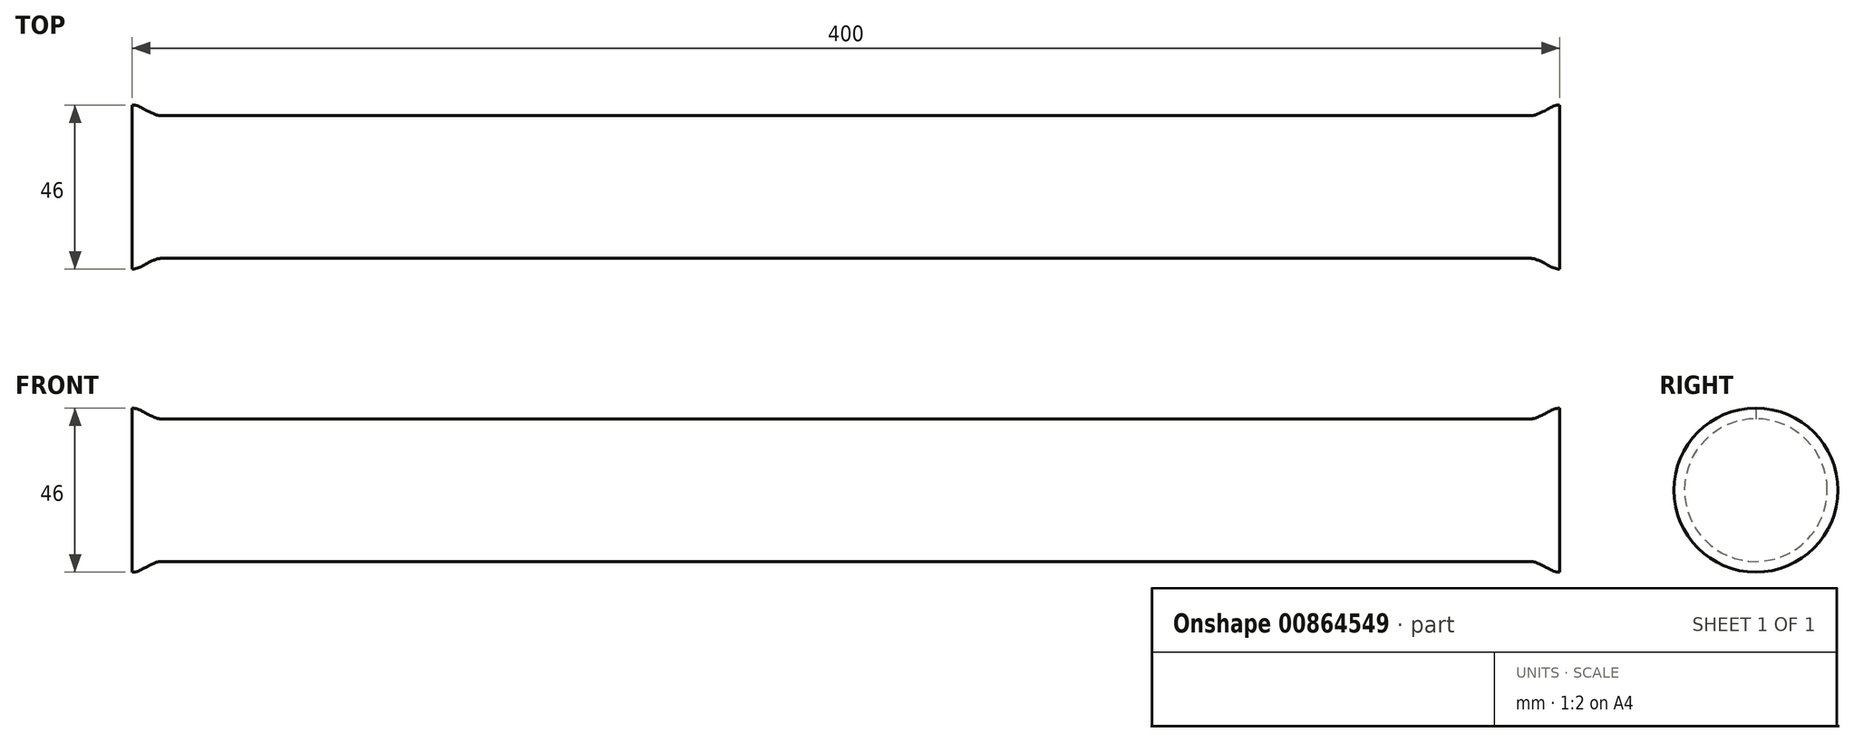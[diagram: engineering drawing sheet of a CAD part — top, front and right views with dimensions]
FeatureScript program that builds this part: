
annotation { "Feature Type Name" : "Feature", "Feature Type Description" : "" }
export const myFeature = defineFeature(function(context is Context, id is Id, definition is map)
    precondition{}
    {
        {
            var Q0;
            Q0=qCreatedBy(makeId("Front.planeOp"),FACE);
            var sketch = newSketch(context, id + "F0", { "sketchPlane" : qUnion([Q0])});
            skLineSegment(sketch, "E0", {"start": v(-200, 0) * mm, "end": v(-200, 23) * mm});
            skLineSegment(sketch, "E1", {"start": v(0, 20) * mm, "end": v(-192, 20) * mm});
            skFitSpline(sketch, "E2", {"points": [v(-200, 23) * mm, v(-196, 21.5) * mm, v(-192, 20) * mm], "startDerivative": vector(9, 0) * mm, "endDerivative": vector(6, 0) * mm});
            skLineSegment(sketch, "E3.MirrorCS", {"start": v(200, 0) * mm, "end": v(200, 23) * mm});
            skFitSpline(sketch, "E4.MirrorCS", {"points": [v(200, 23) * mm, v(196, 21.5) * mm, v(192, 20) * mm], "startDerivative": vector(-9, 0) * mm, "endDerivative": vector(-6, 0) * mm});
            skLineSegment(sketch, "E5.MirrorCS", {"start": v(0, 20) * mm, "end": v(192, 20) * mm});
            skLineSegment(sketch, "E6", {"start": v(-200, 0) * mm, "end": v(200, 0) * mm});
            skSolve(sketch);
        }
        {
            var Q0;
            Q0 = qSketchRegion(id + "F0", true);
            var Q1;
            Q1=sQuery(id+"F0.wireOp",EDGE,"E6");
            revolve(context, id + "F1", {"surfaceOperationType" : NewSurfaceOperationType.NEW, "entities" : qUnion([Q0]), "axis" : qUnion([Q1]), "revolveType" : RevolveType.FULL});
        }
    });
